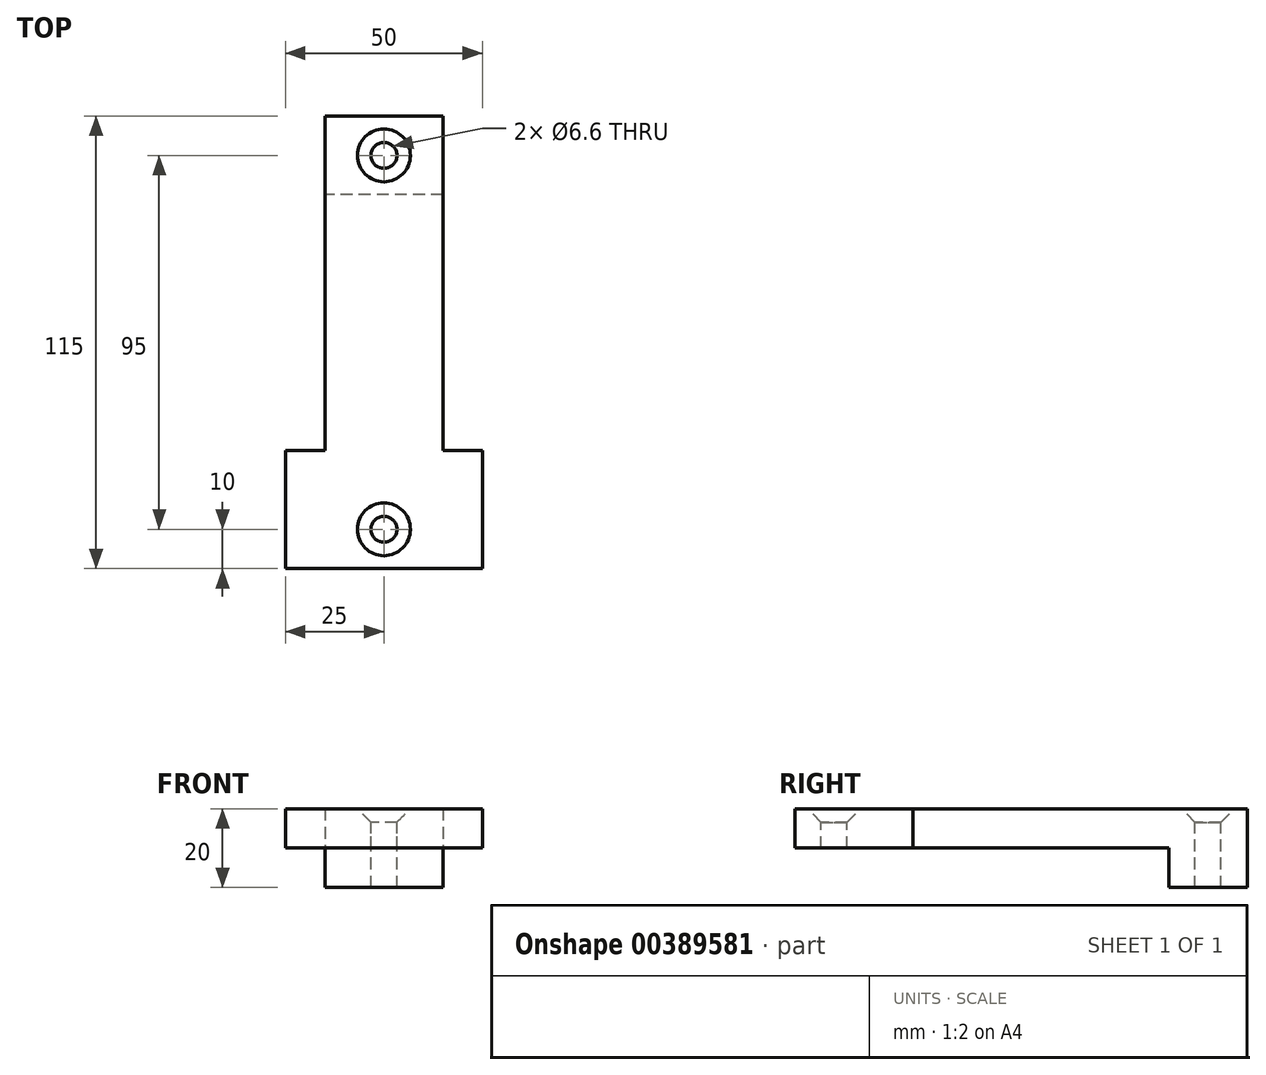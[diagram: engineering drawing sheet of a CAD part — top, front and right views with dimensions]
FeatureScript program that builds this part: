
annotation { "Feature Type Name" : "Feature", "Feature Type Description" : "" }
export const myFeature = defineFeature(function(context is Context, id is Id, definition is map)
    precondition{}
    {
        {
            var Q0;
            Q0=qCreatedBy(makeId("Right.planeOp"),FACE);
            var sketch = newSketch(context, id + "F0", { "sketchPlane" : qUnion([Q0])});
            skLineSegment(sketch, "E0.bottom", {"start": v(10, 10) * mm, "end": v(-10, 10) * mm});
            skLineSegment(sketch, "E0.top", {"start": v(10, -10) * mm, "end": v(-10, -10) * mm});
            skLineSegment(sketch, "E0.left", {"start": v(10, 10) * mm, "end": v(10, -10) * mm});
            skLineSegment(sketch, "E0.right", {"start": v(-10, 0) * mm, "end": v(-10, -10) * mm});
            skPoint(sketch, "E0.middle", {"position": v(0, 0) * mm});
            skLineSegment(sketch, "E1", {"start": v(-10, 10) * mm, "end": v(-75, 10) * mm});
            skLineSegment(sketch, "E2", {"start": v(-75, 10) * mm, "end": v(-75, 0) * mm});
            skLineSegment(sketch, "E3", {"start": v(-75, 0) * mm, "end": v(-10, 0) * mm});
            skSolve(sketch);
        }
        {
            var Q0;
            Q0 = qSketchRegion(id + "F0", true);
            extrude(context, id + "F1", {"entities" : qUnion([Q0]), "endBound" : BoundingType.SYMMETRIC, "depth" : 30 * mm});
        }
        {
            var Q0;
            Q0=makeQuery(id+"F1.opExtrude","SWEPT_FACE",FACE,{"disambiguationData":[OSD([sQuery(id+"F0.wireOp",EDGE,"E2")])]});
            var sketch = newSketch(context, id + "F2", { "sketchPlane" : qUnion([Q0])});
            skLineSegment(sketch, "E4.bottom", {"start": v(-25, 10) * mm, "end": v(25, 10) * mm});
            skLineSegment(sketch, "E4.top", {"start": v(-25, 0) * mm, "end": v(25, 0) * mm});
            skLineSegment(sketch, "E4.left", {"start": v(-25, 10) * mm, "end": v(-25, 0) * mm});
            skLineSegment(sketch, "E4.right", {"start": v(25, 10) * mm, "end": v(25, 0) * mm});
            skSolve(sketch);
        }
        {
            var Q0;
            Q0 = qSketchRegion(id + "F2", true);
            extrude(context, id + "F3", {"entities" : qUnion([Q0]), "operationType" : NewBodyOperationType.ADD, "depth" : 30 * mm});
        }
        {
            var Q0;
            Q0=makeQuery(id+"F3.boolean.opBoolean","MERGE",FACE,{"derivedFrom":[makeQuery(id+"F1.opExtrude","SWEPT_FACE",FACE,{"disambiguationData":[OSD([sQuery(id+"F0.wireOp",EDGE,"E0.bottom"),sQuery(id+"F0.wireOp",EDGE,"E1")])]}),makeQuery(id+"F3.opExtrude","SWEPT_FACE",FACE,{"disambiguationData":[OSD([sQuery(id+"F2.wireOp",EDGE,"E4.bottom")])]})]});
            var sketch = newSketch(context, id + "F4", { "sketchPlane" : qUnion([Q0])});
            skPoint(sketch, "E5", {"position": v(0, 0) * mm});
            skPoint(sketch, "E6", {"position": v(0, -90) * mm});
            skSolve(sketch);
        }
        {
            var Q0;
            Q0=sQuery(id+"F4.wireOp",VERTEX,"E5");
            var Q1;
            Q1=makeQuery(id+"F1.opExtrude","SWEPT_BODY",BODY,{"disambiguationData":[OSD([sQuery(id+"F0.wireOp",EDGE,"E0.bottom"),sQuery(id+"F0.wireOp",EDGE,"E0.top"),sQuery(id+"F0.wireOp",EDGE,"E0.left"),sQuery(id+"F0.wireOp",EDGE,"E0.right"),sQuery(id+"F0.wireOp",EDGE,"E1"),sQuery(id+"F0.wireOp",EDGE,"E2"),sQuery(id+"F0.wireOp",EDGE,"E3")])]});
            hole(context, id + "F5", {"style" : HoleStyle.C_SINK, "endStyle" : HoleEndStyle.BLIND, "standardTappedOrClearance" : lookupTablePath({ "standard" : "ISO", "fit" : "Normal", "size" : "M6", "type" : "Clearance" }), "standardBlindInLast" : lookupTablePath({ "fit" : "Standard", "standard" : "ISO", "size" : "M6", "type" : "Clearance" }), "holeDiameter" : 6.6 * mm, "cSinkDiameter" : 13.44 * mm, "cSinkAngle" : 90 * degree, "holeDepth" : 20 * mm, "isTappedThrough" : true, "tappedDepth" : 20 * mm, "tapClearance" : 0, "startFromSketch" : true, "locations" : qUnion([Q0]), "scope" : qUnion([Q1])});
        }
        {
            var Q0;
            Q0=makeQuery(id+"F3.boolean.opBoolean","MERGE",FACE,{"derivedFrom":[makeQuery(id+"F1.opExtrude","SWEPT_FACE",FACE,{"disambiguationData":[OSD([sQuery(id+"F0.wireOp",EDGE,"E0.bottom"),sQuery(id+"F0.wireOp",EDGE,"E1")])]}),makeQuery(id+"F3.opExtrude","SWEPT_FACE",FACE,{"disambiguationData":[OSD([sQuery(id+"F2.wireOp",EDGE,"E4.bottom")])]})]});
            var sketch = newSketch(context, id + "F6", { "sketchPlane" : qUnion([Q0])});
            skPoint(sketch, "E7", {"position": v(0, -95) * mm});
            skPoint(sketch, "E7.positionSnap0", {"position": v(0, -105) * mm});
            skSolve(sketch);
        }
        {
            var Q0;
            Q0=sQuery(id+"F6.wireOp",VERTEX,"E7");
            var Q1;
            Q1=makeQuery(id+"F1.opExtrude","SWEPT_BODY",BODY,{"disambiguationData":[OSD([sQuery(id+"F0.wireOp",EDGE,"E0.bottom"),sQuery(id+"F0.wireOp",EDGE,"E0.top"),sQuery(id+"F0.wireOp",EDGE,"E0.left"),sQuery(id+"F0.wireOp",EDGE,"E0.right"),sQuery(id+"F0.wireOp",EDGE,"E1"),sQuery(id+"F0.wireOp",EDGE,"E2"),sQuery(id+"F0.wireOp",EDGE,"E3")])]});
            hole(context, id + "F7", {"style" : HoleStyle.C_SINK, "endStyle" : HoleEndStyle.BLIND, "standardTappedOrClearance" : lookupTablePath({ "standard" : "ISO", "fit" : "Normal", "size" : "M6", "type" : "Clearance" }), "standardBlindInLast" : lookupTablePath({ "fit" : "Standard", "standard" : "ISO", "size" : "M6", "type" : "Clearance" }), "holeDiameter" : 6.6 * mm, "cSinkDiameter" : 13.44 * mm, "cSinkAngle" : 90 * degree, "holeDepth" : 10 * mm, "isTappedThrough" : true, "tappedDepth" : 20 * mm, "tapClearance" : 0, "locations" : qUnion([Q0]), "scope" : qUnion([Q1])});
        }
    });
